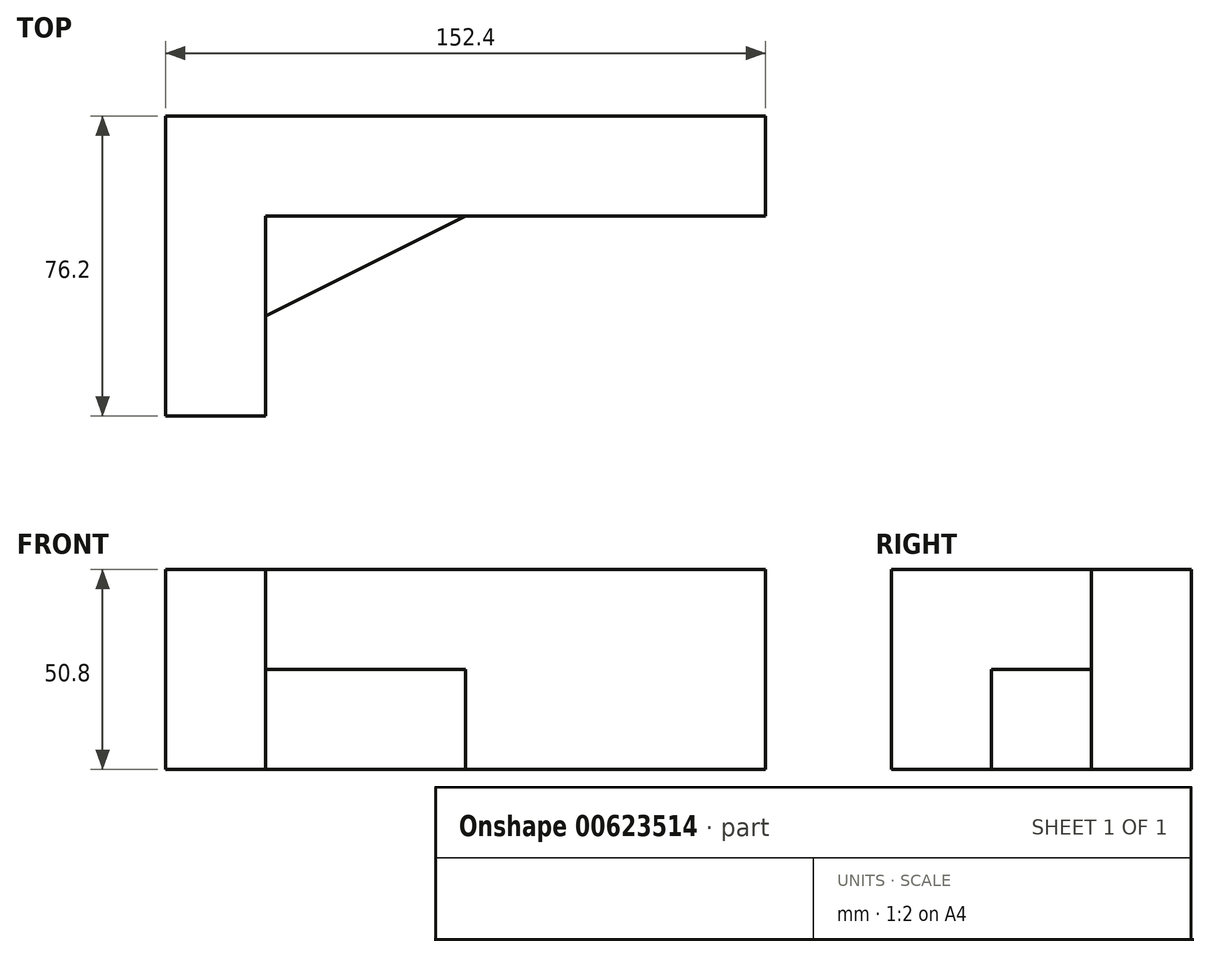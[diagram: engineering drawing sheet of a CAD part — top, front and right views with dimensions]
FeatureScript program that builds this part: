
annotation { "Feature Type Name" : "Feature", "Feature Type Description" : "" }
export const myFeature = defineFeature(function(context is Context, id is Id, definition is map)
    precondition{}
    {
        {
            var Q0;
            Q0=qCreatedBy(makeId("Top.planeOp"),FACE);
            var sketch = newSketch(context, id + "F0", { "sketchPlane" : qUnion([Q0])});
            skLineSegment(sketch, "E0", {"start": v(0, 0) * mm, "end": v(0, 76.2) * mm});
            skLineSegment(sketch, "E1", {"start": v(0, 76.2) * mm, "end": v(152.4, 76.2) * mm});
            skLineSegment(sketch, "E2", {"start": v(152.4, 76.2) * mm, "end": v(152.4, 50.8) * mm});
            skLineSegment(sketch, "E3", {"start": v(152.4, 50.8) * mm, "end": v(25.4, 50.8) * mm});
            skLineSegment(sketch, "E4", {"start": v(25.4, 50.8) * mm, "end": v(25.4, 0) * mm});
            skLineSegment(sketch, "E5", {"start": v(25.4, 0) * mm, "end": v(0, 0) * mm});
            skSolve(sketch);
        }
        {
            var Q0;
            Q0 = qSketchRegion(id + "F0", true);
            extrude(context, id + "F1", {"entities" : qUnion([Q0]), "depth" : 50.8 * mm, "offsetDistance" : 25.4 * mm});
        }
        {
            var Q0;
            Q0=makeQuery(id+"F1.opExtrude","CAP_FACE",FACE,{"disambiguationData":[OSD([sQuery(id+"F0.wireOp",EDGE,"E0"),sQuery(id+"F0.wireOp",EDGE,"E1"),sQuery(id+"F0.wireOp",EDGE,"E2"),sQuery(id+"F0.wireOp",EDGE,"E3"),sQuery(id+"F0.wireOp",EDGE,"E4"),sQuery(id+"F0.wireOp",EDGE,"E5")])],"isStart":false});
            var sketch = newSketch(context, id + "F2", { "sketchPlane" : qUnion([Q0])});
            skLineSegment(sketch, "E6", {"start": v(25.4, 50.8) * mm, "end": v(25.4, 25.4) * mm});
            skLineSegment(sketch, "E7", {"start": v(25.4, 50.8) * mm, "end": v(76.2, 50.8) * mm});
            skLineSegment(sketch, "E8", {"start": v(25.4, 25.4) * mm, "end": v(76.2, 50.8) * mm});
            skSolve(sketch);
        }
        {
            var Q0;
            Q0 = qSketchRegion(id + "F2", true);
            extrude(context, id + "F3", {"entities" : qUnion([Q0]), "operationType" : NewBodyOperationType.ADD, "oppositeDirection" : true, "depth" : 50.8 * mm, "offsetDistance" : 25.4 * mm});
        }
        {
            var Q0;
            Q0=makeQuery(id+"F3.boolean.opBoolean","MERGE",FACE,{"derivedFrom":[makeQuery(id+"F1.opExtrude","CAP_FACE",FACE,{"disambiguationData":[OSD([sQuery(id+"F0.wireOp",EDGE,"E0"),sQuery(id+"F0.wireOp",EDGE,"E1"),sQuery(id+"F0.wireOp",EDGE,"E2"),sQuery(id+"F0.wireOp",EDGE,"E3"),sQuery(id+"F0.wireOp",EDGE,"E4"),sQuery(id+"F0.wireOp",EDGE,"E5")])],"isStart":false}),makeQuery(id+"F3.opExtrude","CAP_FACE",FACE,{"disambiguationData":[OSD([sQuery(id+"F2.wireOp",EDGE,"E6"),sQuery(id+"F2.wireOp",EDGE,"E7"),sQuery(id+"F2.wireOp",EDGE,"E8")])],"isStart":true})]});
            var sketch = newSketch(context, id + "F4", { "sketchPlane" : qUnion([Q0])});
            skLineSegment(sketch, "E9", {"start": v(25.4, 25.4) * mm, "end": v(25.4, 50.8) * mm});
            skLineSegment(sketch, "E10", {"start": v(25.4, 50.8) * mm, "end": v(76.2, 50.8) * mm});
            skSolve(sketch);
        }
        {
            var Q0;
            Q0=makeQuery(id+"F4.imprint","IMPRINT",FACE,{"disambiguationData":[TD([[makeQuery(id+"F4.imprint","IMPRINT",EDGE,{"derivedFrom":sQuery(id+"F4.wireOp",EDGE,"E9")}),-1.0]])]});
            extrude(context, id + "F5", {"entities" : qUnion([Q0]), "operationType" : NewBodyOperationType.REMOVE, "oppositeDirection" : true, "depth" : 25.4 * mm, "offsetDistance" : 25.4 * mm});
        }
    });
